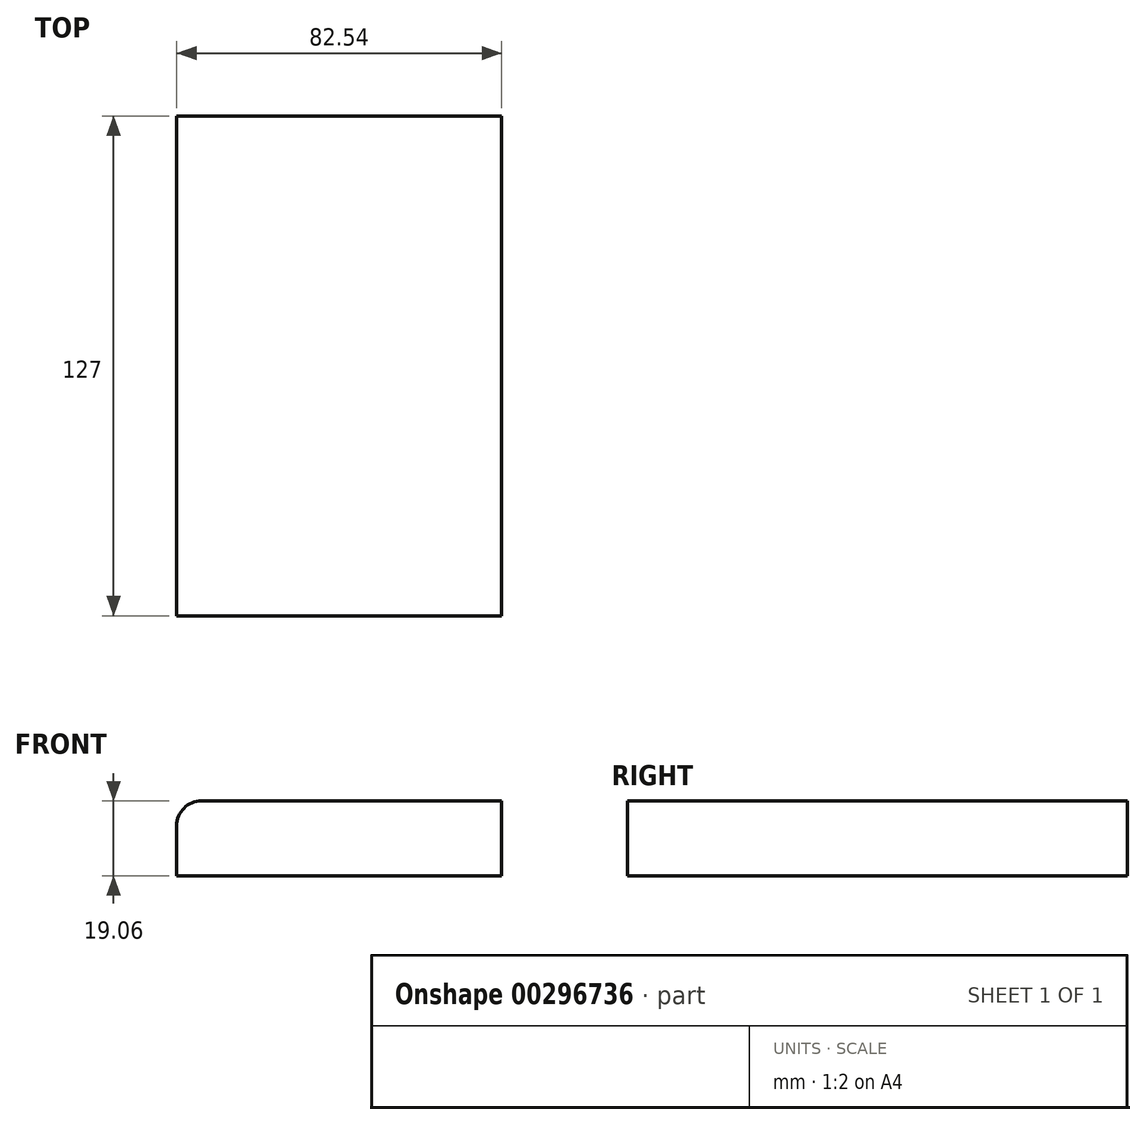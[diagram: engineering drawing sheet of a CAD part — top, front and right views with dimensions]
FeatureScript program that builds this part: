
annotation { "Feature Type Name" : "Feature", "Feature Type Description" : "" }
export const myFeature = defineFeature(function(context is Context, id is Id, definition is map)
    precondition{}
    {
        {
            var Q0;
            Q0=qCreatedBy(makeId("Front.planeOp"),FACE);
            var sketch = newSketch(context, id + "F0", { "sketchPlane" : qUnion([Q0])});
            skLineSegment(sketch, "E0.bottom", {"start": v(41.28, -9.52) * mm, "end": v(-41.28, -9.53) * mm});
            skLineSegment(sketch, "E0.top", {"start": v(41.28, 9.53) * mm, "end": v(-34.93, 9.53) * mm});
            skLineSegment(sketch, "E0.left", {"start": v(41.28, -9.52) * mm, "end": v(41.28, 9.53) * mm});
            skLineSegment(sketch, "E0.right", {"start": v(-41.28, -9.53) * mm, "end": v(-41.28, 3.18) * mm});
            skPoint(sketch, "E0.middle", {"position": v(0, 0) * mm});
            skLineSegment(sketch, "E1.bottom", {"start": v(73.97, 73.43) * mm, "end": v(106.66, 73.43) * mm});
            skLineSegment(sketch, "E1.top", {"start": v(73.97, 44.85) * mm, "end": v(106.66, 44.85) * mm});
            skLineSegment(sketch, "E1.left", {"start": v(73.97, 73.43) * mm, "end": v(73.97, 44.85) * mm});
            skLineSegment(sketch, "E1.right", {"start": v(106.66, 73.43) * mm, "end": v(106.66, 44.85) * mm});
            skPoint(sketch, "E1.middle", {"position": v(90.31, 59.14) * mm});
            skLineSegment(sketch, "E2", {"start": v(41.28, 9.53) * mm, "end": v(41.28, 61.93) * mm});
            skArc(sketch, "E3", {"start": v(41.27, 61.93) * mm, "mid": v(47.04, 74.16) * mm, "end": v(60.15, 77.51) * mm});
            skLineSegment(sketch, "E4", {"start": v(61.35, 77.4) * mm, "end": v(111.49, 77.4) * mm});
            skLineSegment(sketch, "E5.0", {"start": v(62.4, 96.17) * mm, "end": v(111.49, 96.17) * mm});
            skArc(sketch, "E5.1", {"start": v(22.5, 61.93) * mm, "mid": v(34.58, 88.21) * mm, "end": v(62.4, 96.17) * mm});
            skLineSegment(sketch, "E5.2", {"start": v(22.5, 9.53) * mm, "end": v(22.5, 61.93) * mm});
            skPoint(sketch, "E6.visualSharp", {"position": v(60.69, 77.4) * mm});
            skArc(sketch, "E6.filletArc", {"start": v(60.15, 77.51) * mm, "mid": v(60.74, 77.43) * mm, "end": v(61.35, 77.4) * mm});
            skPoint(sketch, "E7.visualSharp", {"position": v(-41.28, 9.53) * mm});
            skArc(sketch, "E7.filletArc", {"start": v(-34.93, 9.53) * mm, "mid": v(-39.42, 7.67) * mm, "end": v(-41.28, 3.18) * mm});
            skSolve(sketch);
        }
        {
            var Q0;
            Q0=makeQuery(id+"F0.imprint","IMPRINT",FACE,{"disambiguationData":[TD([[makeQuery(id+"F0.imprint","IMPRINT",EDGE,{"derivedFrom":sQuery(id+"F0.wireOp",EDGE,"E0.bottom")}),-1.0]])]});
            extrude(context, id + "F1", {"entities" : qUnion([Q0]), "endBound" : BoundingType.SYMMETRIC, "depth" : 127 * mm});
        }
    });
